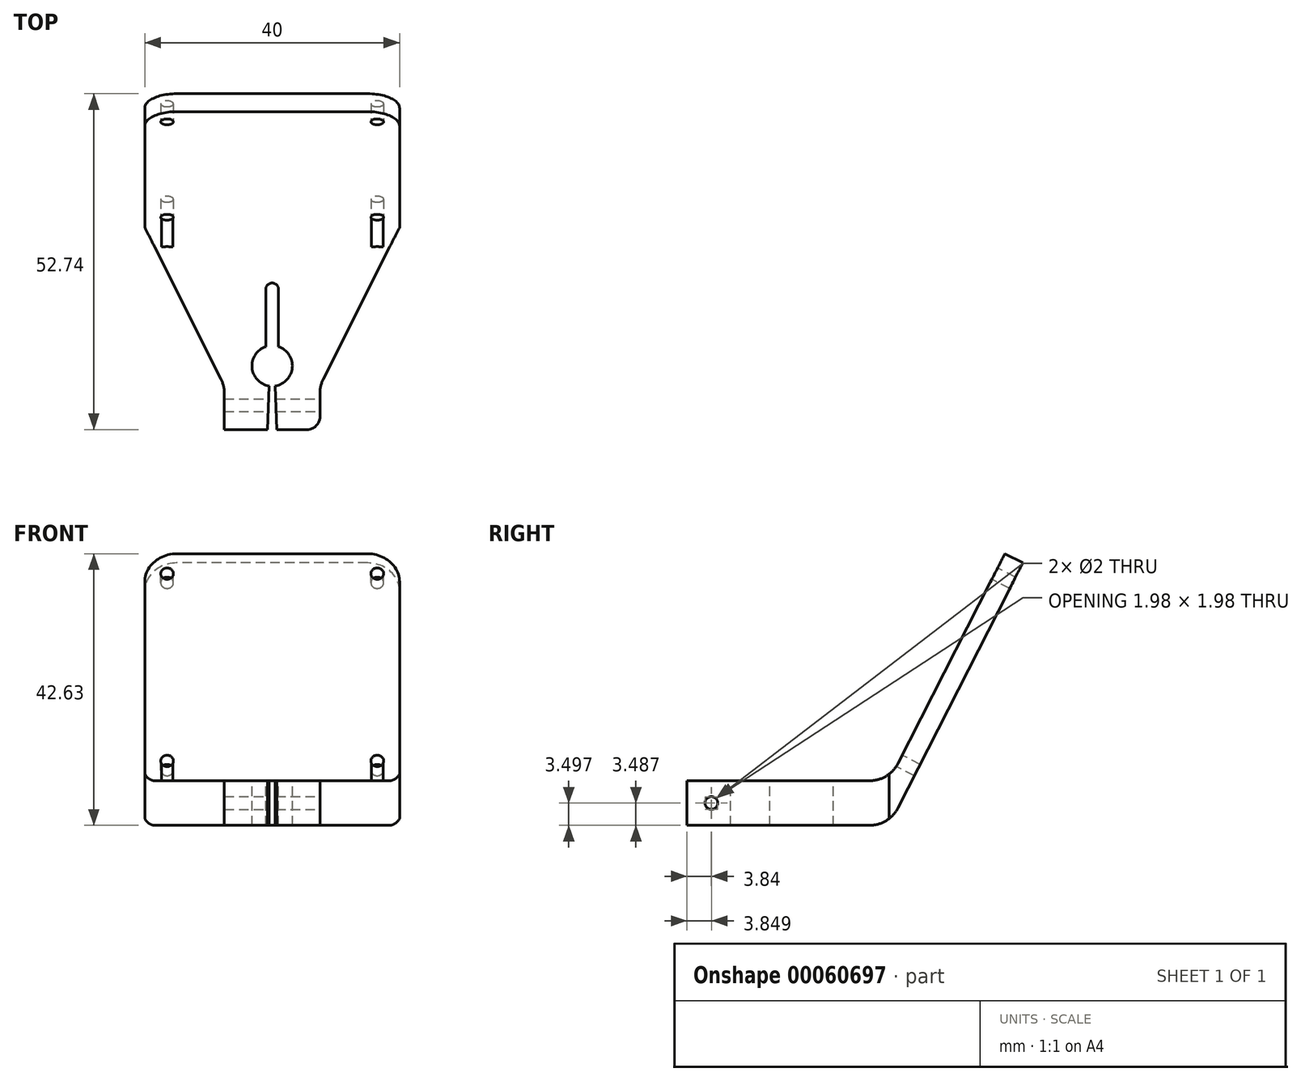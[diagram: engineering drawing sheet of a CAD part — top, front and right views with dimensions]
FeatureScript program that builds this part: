
annotation { "Feature Type Name" : "Feature", "Feature Type Description" : "" }
export const myFeature = defineFeature(function(context is Context, id is Id, definition is map)
    precondition{}
    {
        {
            var Q0;
            Q0=qCreatedBy(makeId("Right.planeOp"),FACE);
            var sketch = newSketch(context, id + "F0", { "sketchPlane" : qUnion([Q0])});
            skLineSegment(sketch, "E0", {"start": v(-31.75, 0) * mm, "end": v(0, 0) * mm});
            skLineSegment(sketch, "E1", {"start": v(0, 0) * mm, "end": v(20.99, 41.2) * mm});
            skLineSegment(sketch, "E2", {"start": v(20.99, 41.2) * mm, "end": v(18.16, 42.63) * mm});
            skLineSegment(sketch, "E3", {"start": v(18.16, 42.63) * mm, "end": v(0, 7) * mm});
            skLineSegment(sketch, "E4", {"start": v(0, 7) * mm, "end": v(-31.75, 7) * mm});
            skLineSegment(sketch, "E5", {"start": v(-31.75, 7) * mm, "end": v(-31.75, 0) * mm});
            skSolve(sketch);
        }
        {
            var Q0;
            Q0 = qSketchRegion(id + "F0", true);
            extrude(context, id + "F1", {"entities" : qUnion([Q0]), "endBound" : BoundingType.SYMMETRIC, "depth" : 40 * mm});
        }
        {
            var Q0;
            Q0=makeQuery(id+"F1.opExtrude","SWEPT_FACE",FACE,{"disambiguationData":[OSD([sQuery(id+"F0.wireOp",EDGE,"E3")])]});
            var sketch = newSketch(context, id + "F2", { "sketchPlane" : qUnion([Q0])});
            skPoint(sketch, "E6", {"position": v(-16.5, 42.73) * mm});
            skPoint(sketch, "E7", {"position": v(16.5, 42.73) * mm});
            skPoint(sketch, "E8", {"position": v(-16.5, 9.73) * mm});
            skPoint(sketch, "E9", {"position": v(16.5, 9.73) * mm});
            skLineSegment(sketch, "E10", {"start": v(0, 46.23) * mm, "end": v(0, 26.23) * mm, "construction": true});
            skPoint(sketch, "E10.endSnap0", {"position": v(0, 46.23) * mm});
            skLineSegment(sketch, "E11", {"start": v(0, 26.23) * mm, "end": v(20, 26.23) * mm, "construction": true});
            skSolve(sketch);
        }
        {
            var Q0;
            Q0=sQuery(id+"F2.wireOp",VERTEX,"E6");
            var Q1;
            Q1=sQuery(id+"F2.wireOp",VERTEX,"E7");
            var Q2;
            Q2=sQuery(id+"F2.wireOp",VERTEX,"E8");
            var Q3;
            Q3=sQuery(id+"F2.wireOp",VERTEX,"E9");
            var Q4;
            Q4=makeQuery(id+"F1.opExtrude","SWEPT_BODY",BODY,{"disambiguationData":[OSD([sQuery(id+"F0.wireOp",EDGE,"E0"),sQuery(id+"F0.wireOp",EDGE,"E1"),sQuery(id+"F0.wireOp",EDGE,"E2"),sQuery(id+"F0.wireOp",EDGE,"E3"),sQuery(id+"F0.wireOp",EDGE,"E4"),sQuery(id+"F0.wireOp",EDGE,"E5")])]});
            hole(context, id + "F3", {"style" : HoleStyle.SIMPLE, "holeDiameter" : 2 * mm, "endStyle" : HoleEndStyle.THROUGH, "locations" : qUnion([Q0, Q1, Q2, Q3]), "scope" : qUnion([Q4])});
        }
        {
            var Q0;
            Q0=makeQuery(id+"F1.opExtrude","SWEPT_FACE",FACE,{"disambiguationData":[OSD([sQuery(id+"F0.wireOp",EDGE,"E4")])]});
            var sketch = newSketch(context, id + "F4", { "sketchPlane" : qUnion([Q0])});
            skLineSegment(sketch, "E12", {"start": v(20, 0) * mm, "end": v(7.5, -24.89) * mm});
            skLineSegment(sketch, "E13", {"start": v(-7.5, -24.89) * mm, "end": v(-20, 0) * mm});
            skLineSegment(sketch, "E14", {"start": v(-20, 0) * mm, "end": v(-20, -38.64) * mm});
            skLineSegment(sketch, "E15", {"start": v(-20, -38.64) * mm, "end": v(20, -38.64) * mm});
            skLineSegment(sketch, "E16", {"start": v(20, -38.64) * mm, "end": v(20, 0) * mm});
            skArc(sketch, "E17", {"start": v(0.5, -24.89) * mm, "mid": v(3.16, -22) * mm, "end": v(1, -18.74) * mm});
            skLineSegment(sketch, "E18", {"start": v(-7.5, -31.75) * mm, "end": v(-0.75, -31.75) * mm});
            skLineSegment(sketch, "E19", {"start": v(-0.75, -31.75) * mm, "end": v(-0.5, -24.89) * mm});
            skLineSegment(sketch, "E20", {"start": v(0.5, -24.89) * mm, "end": v(0.75, -31.75) * mm});
            skLineSegment(sketch, "E21", {"start": v(0.75, -31.75) * mm, "end": v(7.5, -31.75) * mm});
            skLineSegment(sketch, "E22", {"start": v(7.5, -31.75) * mm, "end": v(7.5, -24.89) * mm});
            skLineSegment(sketch, "E23", {"start": v(-7.5, -31.75) * mm, "end": v(-7.5, -24.89) * mm});
            skLineSegment(sketch, "E24.top", {"start": v(0, -8.74) * mm, "end": v(0, -8.74) * mm});
            skLineSegment(sketch, "E24.left", {"start": v(-1, -18.74) * mm, "end": v(-1, -9.74) * mm});
            skLineSegment(sketch, "E24.right", {"start": v(1, -18.74) * mm, "end": v(1, -9.74) * mm});
            skLineSegment(sketch, "E25", {"start": v(0, 0) * mm, "end": v(0, -45.6) * mm, "construction": true});
            skPoint(sketch, "E26", {"position": v(0, -8.74) * mm});
            skArc(sketch, "E27.trimOffspring", {"start": v(-1, -18.74) * mm, "mid": v(-3.16, -22) * mm, "end": v(-0.5, -24.89) * mm});
            skPoint(sketch, "E28.visualSharp", {"position": v(-1, -8.74) * mm});
            skArc(sketch, "E28.filletArc", {"start": v(0, -8.74) * mm, "mid": v(-0.7, -9.03) * mm, "end": v(-1, -9.74) * mm});
            skPoint(sketch, "E29.visualSharp", {"position": v(1, -8.74) * mm});
            skArc(sketch, "E29.filletArc", {"start": v(1, -9.74) * mm, "mid": v(0.7, -9.03) * mm, "end": v(0, -8.74) * mm});
            skSolve(sketch);
        }
        {
            var Q0;
            Q0 = qSketchRegion(id + "F4", true);
            extrude(context, id + "F5", {"entities" : qUnion([Q0]), "operationType" : NewBodyOperationType.REMOVE, "endBound" : BoundingType.THROUGH_ALL, "oppositeDirection" : true, "depth" : 25 * mm});
        }
        {
            var Q0;
            Q0=makeQuery(id+"F1.opExtrude","CAP_EDGE",EDGE,{"disambiguationData":[OSD([sQuery(id+"F0.wireOp",EDGE,"E2")])],"isStart":false});
            var Q1;
            Q1=makeQuery(id+"F1.opExtrude","CAP_EDGE",EDGE,{"disambiguationData":[OSD([sQuery(id+"F0.wireOp",EDGE,"E2")])],"isStart":true});
            var Q2;
            Q2=makeQuery(id+"F5.boolean.opBoolean","COPY",EDGE,{"derivedFrom":makeQuery(id+"F5.opExtrude","SWEPT_EDGE",EDGE,{"disambiguationData":[OSD([sQuery(id+"F0.wireOp",EDGE,"E3"),sQuery(id+"F0.wireOp",EDGE,"E4"),sQuery(id+"F4.wireOp",EDGE,"E13"),sQuery(id+"F4.wireOp",EDGE,"E14")])]})});
            var Q3;
            Q3=makeQuery(id+"F5.boolean.opBoolean","COPY",EDGE,{"derivedFrom":makeQuery(id+"F5.opExtrude","SWEPT_EDGE",EDGE,{"disambiguationData":[OSD([sQuery(id+"F4.wireOp",EDGE,"E13"),sQuery(id+"F4.wireOp",EDGE,"E23")])]})});
            var Q4;
            Q4=makeQuery(id+"F5.boolean.opBoolean","COPY",EDGE,{"derivedFrom":makeQuery(id+"F5.opExtrude","SWEPT_EDGE",EDGE,{"disambiguationData":[OSD([sQuery(id+"F4.wireOp",EDGE,"E12"),sQuery(id+"F4.wireOp",EDGE,"E22")])]})});
            var Q5;
            Q5=makeQuery(id+"F5.boolean.opBoolean","COPY",EDGE,{"derivedFrom":makeQuery(id+"F5.opExtrude","SWEPT_EDGE",EDGE,{"disambiguationData":[OSD([sQuery(id+"F0.wireOp",EDGE,"E3"),sQuery(id+"F0.wireOp",EDGE,"E4"),sQuery(id+"F4.wireOp",EDGE,"E12"),sQuery(id+"F4.wireOp",EDGE,"E16")])]})});
            var Q6;
            Q6=makeQuery(id+"F1.opExtrude","SWEPT_EDGE",EDGE,{"disambiguationData":[OSD([sQuery(id+"F0.wireOp",EDGE,"E3"),sQuery(id+"F0.wireOp",EDGE,"E4")])]});
            var Q7;
            Q7=makeQuery(id+"F1.opExtrude","SWEPT_EDGE",EDGE,{"disambiguationData":[OSD([sQuery(id+"F0.wireOp",EDGE,"E0"),sQuery(id+"F0.wireOp",EDGE,"E1")])]});
            fillet(context, id + "F6", {"entities" : qUnion([Q0, Q1, Q2, Q3, Q4, Q5, Q6, Q7]), "radius" : 5 * mm, "tangentPropagation" : true, "allowEdgeOverflow" : false});
        }
        {
            var Q0;
            Q0=makeQuery(id+"F5.boolean.opBoolean","COPY",EDGE,{"derivedFrom":makeQuery(id+"F5.opExtrude","SWEPT_EDGE",EDGE,{"disambiguationData":[OSD([sQuery(id+"F0.wireOp",EDGE,"E4"),sQuery(id+"F0.wireOp",EDGE,"E5"),sQuery(id+"F4.wireOp",EDGE,"E21"),sQuery(id+"F4.wireOp",EDGE,"E22")])]})});
            var Q1;
            Q1=makeQuery(id+"F5.boolean.opBoolean","COPY",EDGE,{"derivedFrom":makeQuery(id+"F5.opExtrude","SWEPT_EDGE",EDGE,{"disambiguationData":[OSD([sQuery(id+"F0.wireOp",EDGE,"E4"),sQuery(id+"F0.wireOp",EDGE,"E5"),sQuery(id+"F4.wireOp",EDGE,"E18"),sQuery(id+"F4.wireOp",EDGE,"E23")])]})});
            fillet(context, id + "F7", {"entities" : qUnion([Q0, Q1]), "radius" : 2 * mm, "tangentPropagation" : true, "allowEdgeOverflow" : false});
        }
        {
            var Q0;
            Q0=makeQuery(id+"F5.boolean.opBoolean","COPY",FACE,{"derivedFrom":makeQuery(id+"F5.opExtrude","SWEPT_FACE",FACE,{"disambiguationData":[OSD([sQuery(id+"F4.wireOp",EDGE,"E22")])]})});
            var sketch = newSketch(context, id + "F8", { "sketchPlane" : qUnion([Q0])});
            skPoint(sketch, "E30", {"position": v(-27.91, 3.5) * mm});
            skPoint(sketch, "E30.positionSnap0", {"position": v(-27.91, 7) * mm});
            skPoint(sketch, "E30.positionSnap1", {"position": v(-26.07, 3.5) * mm});
            skSolve(sketch);
        }
        {
            var Q0;
            Q0=sQuery(id+"F8.wireOp",VERTEX,"E30");
            var Q1;
            Q1=makeQuery(id+"F1.opExtrude","SWEPT_BODY",BODY,{"disambiguationData":[OSD([sQuery(id+"F0.wireOp",EDGE,"E0"),sQuery(id+"F0.wireOp",EDGE,"E1"),sQuery(id+"F0.wireOp",EDGE,"E2"),sQuery(id+"F0.wireOp",EDGE,"E3"),sQuery(id+"F0.wireOp",EDGE,"E4"),sQuery(id+"F0.wireOp",EDGE,"E5")])]});
            hole(context, id + "F9", {"style" : HoleStyle.SIMPLE, "holeDiameter" : 2 * mm, "endStyle" : HoleEndStyle.THROUGH, "locations" : qUnion([Q0]), "scope" : qUnion([Q1])});
        }
    });
